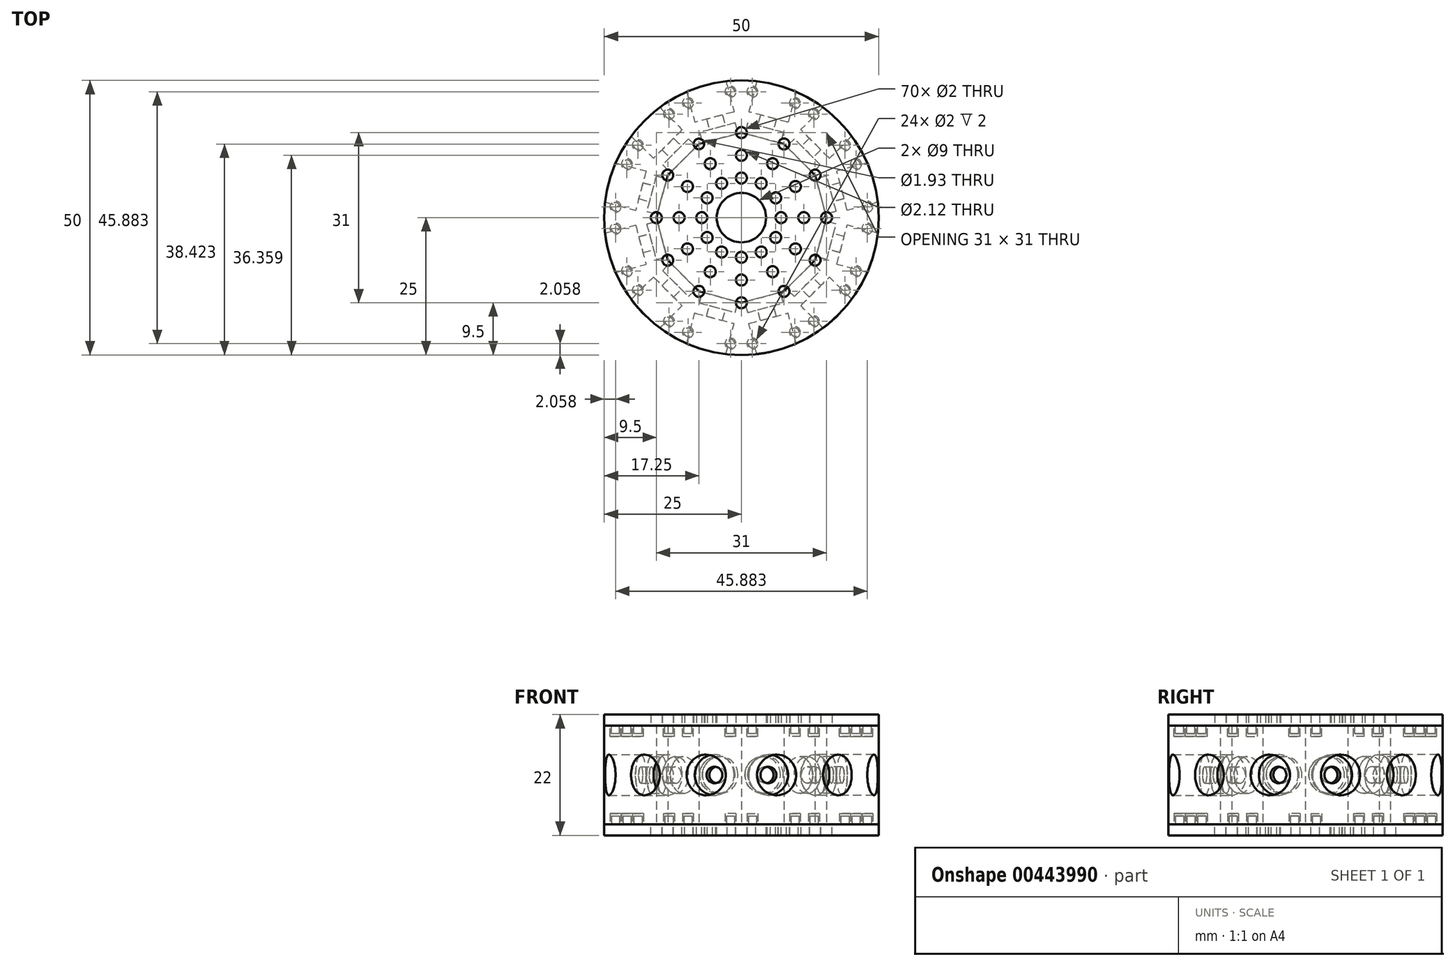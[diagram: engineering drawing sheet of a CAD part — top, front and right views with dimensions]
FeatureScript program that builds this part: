
annotation { "Feature Type Name" : "Feature", "Feature Type Description" : "" }
export const myFeature = defineFeature(function(context is Context, id is Id, definition is map)
    precondition{}
    {
        {
            var Q0;
            Q0=qCreatedBy(makeId("Top.planeOp"),FACE);
            var sketch = newSketch(context, id + "F0", { "sketchPlane" : qUnion([Q0])});
            skCircle(sketch, "E0", {"center": v(0, 0) * mm, "radius": 15.5 * mm, "construction": true});
            skCircle(sketch, "E1", {"center": v(0, 0) * mm, "radius": 25 * mm});
            skLineSegment(sketch, "E2", {"start": v(0, 0) * mm, "end": v(0, 25) * mm});
            skLineSegment(sketch, "E3", {"start": v(0, 0) * mm, "end": v(12.5, 21.65) * mm});
            skLineSegment(sketch, "E4", {"start": v(0, 15.5) * mm, "end": v(7.75, 13.42) * mm});
            skLineSegment(sketch, "E5", {"start": v(7.75, 13.42) * mm, "end": v(13.42, 7.75) * mm});
            skLineSegment(sketch, "E6", {"start": v(13.42, 7.75) * mm, "end": v(15.5, 0) * mm});
            skLineSegment(sketch, "E7", {"start": v(7.75, -13.42) * mm, "end": v(0, -15.5) * mm});
            skLineSegment(sketch, "E8", {"start": v(0, -15.5) * mm, "end": v(-7.75, -13.42) * mm});
            skLineSegment(sketch, "E9", {"start": v(-7.75, -13.42) * mm, "end": v(-13.42, -7.75) * mm});
            skLineSegment(sketch, "E10", {"start": v(-13.42, -7.75) * mm, "end": v(-15.5, 0) * mm});
            skLineSegment(sketch, "E11", {"start": v(-13.42, 7.75) * mm, "end": v(-7.75, 13.42) * mm});
            skLineSegment(sketch, "E12", {"start": v(-7.75, 13.42) * mm, "end": v(0, 15.5) * mm});
            skLineSegment(sketch, "E13", {"start": v(-13.42, 7.75) * mm, "end": v(-15.5, 0) * mm});
            skLineSegment(sketch, "E14.MirrorCS", {"start": v(0, 0) * mm, "end": v(-12.5, 21.65) * mm, "construction": true});
            skLineSegment(sketch, "E15.MirrorCS", {"start": v(0, 0) * mm, "end": v(-21.65, 12.5) * mm, "construction": true});
            skLineSegment(sketch, "E16.MirrorCS", {"start": v(0, 0) * mm, "end": v(-25, 0) * mm, "construction": true});
            skLineSegment(sketch, "E17.MirrorCS", {"start": v(0, 0) * mm, "end": v(-21.65, -12.5) * mm, "construction": true});
            skLineSegment(sketch, "E18.MirrorCS", {"start": v(0, 0) * mm, "end": v(-12.5, -21.65) * mm, "construction": true});
            skLineSegment(sketch, "E19.MirrorCS", {"start": v(0, 0) * mm, "end": v(0, -25) * mm, "construction": true});
            skLineSegment(sketch, "E20.MirrorCS", {"start": v(0, 0) * mm, "end": v(12.5, -21.65) * mm, "construction": true});
            skLineSegment(sketch, "E21.MirrorCS", {"start": v(0, 0) * mm, "end": v(21.65, -12.5) * mm, "construction": true});
            skLineSegment(sketch, "E22.MirrorCS", {"start": v(0, 0) * mm, "end": v(25, 0) * mm, "construction": true});
            skLineSegment(sketch, "E23.MirrorCS", {"start": v(0, 0) * mm, "end": v(21.65, 12.5) * mm, "construction": true});
            skLineSegment(sketch, "E24", {"start": v(7.75, -13.42) * mm, "end": v(13.42, -7.75) * mm});
            skLineSegment(sketch, "E25", {"start": v(13.42, -7.75) * mm, "end": v(15.5, 0) * mm});
            skLineSegment(sketch, "E26", {"start": v(0, 0) * mm, "end": v(14.97, 4.01) * mm, "construction": true});
            skSolve(sketch);
        }
        {
            var Q0;
            {var subQ5=sQuery(id+"F0.wireOp",EDGE,"E4");Q0=makeQuery(id+"F0.imprint","IMPRINT",FACE,{"disambiguationData":[TD([[makeQuery(id+"F0.imprint","IMPRINT",EDGE,{"derivedFrom":subQ5}),1.0]])]});}
            extrude(context, id + "F1", {"entities" : qUnion([Q0]), "depth" : 18 * mm});
        }
        {
            var Q0;
            Q0=makeQuery(id+"F1.opExtrude","SWEPT_FACE",FACE,{"disambiguationData":[OSD([sQuery(id+"F0.wireOp",EDGE,"E4")])]});
            var sketch = newSketch(context, id + "F2", { "sketchPlane" : qUnion([Q0])});
            skLineSegment(sketch, "E27.0", {"start": v(-4.01, 18) * mm, "end": v(4.01, 18) * mm});
            skLineSegment(sketch, "E27.1", {"start": v(-4.01, 18) * mm, "end": v(-4.01, 0) * mm});
            skLineSegment(sketch, "E27.2", {"start": v(-4.01, 0) * mm, "end": v(4.01, 0) * mm});
            skLineSegment(sketch, "E27.3", {"start": v(4.01, 18) * mm, "end": v(4.01, 0) * mm});
            skLineSegment(sketch, "E28", {"start": v(-4.01, 18) * mm, "end": v(4.01, 0) * mm, "construction": true});
            skLineSegment(sketch, "E29", {"start": v(-4.01, 0) * mm, "end": v(4.01, 18) * mm, "construction": true});
            skCircle(sketch, "E30", {"center": v(0, 9) * mm, "radius": 3.35 * mm});
            skCircle(sketch, "E31", {"center": v(0, 9) * mm, "radius": 1.5 * mm});
            skSolve(sketch);
        }
        {
            var Q0;
            Q0=makeQuery(id+"F2.imprint","IMPRINT",FACE,{"disambiguationData":[TD([[makeQuery(id+"F2.imprint","IMPRINT",EDGE,{"derivedFrom":sQuery(id+"F2.wireOp",EDGE,"E30")}),1.0]])]});
            extrude(context, id + "F3", {"entities" : qUnion([Q0]), "operationType" : NewBodyOperationType.REMOVE, "oppositeDirection" : true, "depth" : 2 * mm});
        }
        {
            var Q0;
            Q0=makeQuery(id+"F3.boolean.opBoolean","SPLIT",FACE,{"disambiguationData":[TD([makeQuery(id+"F3.opExtrude","SWEPT_FACE",FACE,{"disambiguationData":[OSD([sQuery(id+"F2.wireOp",EDGE,"E31")])]})])],"derivedFrom":makeQuery(id+"F1.opExtrude","SWEPT_FACE",FACE,{"disambiguationData":[OSD([sQuery(id+"F0.wireOp",EDGE,"E4")])]})});
            extrude(context, id + "F4", {"entities" : qUnion([Q0]), "operationType" : NewBodyOperationType.REMOVE, "oppositeDirection" : true, "depth" : 12 * mm});
        }
        {
            var Q0;
            {var subQ1=sQuery(id+"F0.wireOp",EDGE,"E2");var subQ2=sQuery(id+"F0.wireOp",EDGE,"E4");Q0=makeQuery(id+"F3.boolean.opBoolean","SPLIT",FACE,{"disambiguationData":[TD([makeQuery(id+"F1.opExtrude","SWEPT_FACE",FACE,{"disambiguationData":[OSD([subQ1])]})])],"derivedFrom":makeQuery(id+"F1.opExtrude","SWEPT_FACE",FACE,{"disambiguationData":[OSD([subQ2])]})});}
            cPlane(context, id + "F5", {"entities" : qUnion([Q0]), "cplaneType" : CPlaneType.OFFSET, "offset" : 4 * mm, "oppositeDirection" : true, "width" : 150 * mm, "height" : 150 * mm});
        }
        {
            var Q0;
            Q0=qCreatedBy(id+"F5.planeOp",FACE);
            var sketch = newSketch(context, id + "F6", { "sketchPlane" : qUnion([Q0])});
            skLineSegment(sketch, "E32.0", {"start": v(-4.01, 18) * mm, "end": v(4.01, 18) * mm});
            skLineSegment(sketch, "E32.1", {"start": v(-4.01, 18) * mm, "end": v(-4.01, 0) * mm});
            skLineSegment(sketch, "E32.2", {"start": v(-4.01, 0) * mm, "end": v(4.01, 0) * mm});
            skLineSegment(sketch, "E32.3", {"start": v(4.01, 18) * mm, "end": v(4.01, 0) * mm});
            skLineSegment(sketch, "E33", {"start": v(-4.01, 18) * mm, "end": v(4.01, 0) * mm, "construction": true});
            skLineSegment(sketch, "E34", {"start": v(-4.01, 0) * mm, "end": v(4.01, 18) * mm, "construction": true});
            skCircle(sketch, "E35", {"center": v(0, 9) * mm, "radius": 3.7 * mm});
            skSolve(sketch);
        }
        {
            var Q0;
            Q0=makeQuery(id+"F6.imprint","IMPRINT",FACE,{"disambiguationData":[TD([[makeQuery(id+"F6.imprint","IMPRINT",EDGE,{"derivedFrom":sQuery(id+"F6.wireOp",EDGE,"E35")}),1.0]])]});
            extrude(context, id + "F7", {"entities" : qUnion([Q0]), "operationType" : NewBodyOperationType.REMOVE, "oppositeDirection" : true, "depth" : 12 * mm});
        }
        {
            var Q0;
            Q0=makeQuery(id+"F1.opExtrude","CAP_FACE",FACE,{"disambiguationData":[OSD([sQuery(id+"F0.wireOp",EDGE,"E1"),sQuery(id+"F0.wireOp",EDGE,"E2"),sQuery(id+"F0.wireOp",EDGE,"E3"),sQuery(id+"F0.wireOp",EDGE,"E4")])],"isStart":false});
            var sketch = newSketch(context, id + "F8", { "sketchPlane" : qUnion([Q0])});
            skArc(sketch, "E36.0", {"start": v(12.5, 21.65) * mm, "mid": v(6.47, 24.15) * mm, "end": v(0, 25) * mm, "construction": true});
            skLineSegment(sketch, "E36.1", {"start": v(0, 15.5) * mm, "end": v(0, 25) * mm, "construction": true});
            skLineSegment(sketch, "E36.2", {"start": v(0, 15.5) * mm, "end": v(7.75, 13.42) * mm, "construction": true});
            skLineSegment(sketch, "E36.3", {"start": v(7.75, 13.42) * mm, "end": v(12.5, 21.65) * mm, "construction": true});
            skLineSegment(sketch, "E37", {"start": v(0, 15.5) * mm, "end": v(2.51, 24.87) * mm, "construction": true});
            skLineSegment(sketch, "E38", {"start": v(7.75, 13.42) * mm, "end": v(10.26, 22.8) * mm, "construction": true});
            skLineSegment(sketch, "E39", {"start": v(10.26, 22.8) * mm, "end": v(2.51, 24.87) * mm, "construction": true});
            skLineSegment(sketch, "E40", {"start": v(2, 22.94) * mm, "end": v(9.74, 20.87) * mm, "construction": true});
            skCircle(sketch, "E41", {"center": v(9.74, 20.87) * mm, "radius": 1 * mm});
            skSolve(sketch);
        }
        {
            var Q0;
            Q0=makeQuery(id+"F8.imprint","IMPRINT",FACE,{"disambiguationData":[TD([[makeQuery(id+"F8.imprint","IMPRINT",EDGE,{"derivedFrom":sQuery(id+"F8.wireOp",EDGE,"E41")}),1.0]])]});
            var Q1;
            Q1=sQuery(id+"F8.wireOp",EDGE,"E41");
            extrude(context, id + "F9", {"entities" : qUnion([Q0]), "operationType" : NewBodyOperationType.REMOVE, "surfaceEntities" : qUnion([Q1]), "oppositeDirection" : true, "depth" : 2 * mm});
        }
        {
            var Q0;
            Q0=makeQuery(id+"F1.opExtrude","CAP_FACE",FACE,{"disambiguationData":[OSD([sQuery(id+"F0.wireOp",EDGE,"E1"),sQuery(id+"F0.wireOp",EDGE,"E2"),sQuery(id+"F0.wireOp",EDGE,"E3"),sQuery(id+"F0.wireOp",EDGE,"E4")])],"isStart":true});
            var sketch = newSketch(context, id + "F10", { "sketchPlane" : qUnion([Q0])});
            skArc(sketch, "E42.0", {"start": v(12.5, -21.65) * mm, "mid": v(6.47, -24.15) * mm, "end": v(0, -25) * mm, "construction": true});
            skLineSegment(sketch, "E42.1", {"start": v(7.75, -13.42) * mm, "end": v(12.5, -21.65) * mm, "construction": true});
            skLineSegment(sketch, "E42.2", {"start": v(0, -15.5) * mm, "end": v(7.75, -13.42) * mm, "construction": true});
            skLineSegment(sketch, "E42.3", {"start": v(0, -15.5) * mm, "end": v(0, -25) * mm, "construction": true});
            skLineSegment(sketch, "E43", {"start": v(7.75, -13.42) * mm, "end": v(10.26, -22.8) * mm, "construction": true});
            skLineSegment(sketch, "E44", {"start": v(0, -15.5) * mm, "end": v(2.51, -24.87) * mm, "construction": true});
            skLineSegment(sketch, "E45", {"start": v(2.51, -24.87) * mm, "end": v(10.26, -22.8) * mm, "construction": true});
            skLineSegment(sketch, "E46", {"start": v(9.74, -20.87) * mm, "end": v(2, -22.94) * mm, "construction": true});
            skCircle(sketch, "E47", {"center": v(2, -22.94) * mm, "radius": 1 * mm});
            skSolve(sketch);
        }
        {
            var Q0;
            Q0=makeQuery(id+"F10.imprint","IMPRINT",FACE,{"disambiguationData":[TD([[makeQuery(id+"F10.imprint","IMPRINT",EDGE,{"derivedFrom":sQuery(id+"F10.wireOp",EDGE,"E47")}),1.0]])]});
            extrude(context, id + "F11", {"entities" : qUnion([Q0]), "operationType" : NewBodyOperationType.REMOVE, "oppositeDirection" : true, "depth" : 2 * mm});
        }
        {
            var Q0;
            Q0=makeQuery(id+"F1.opExtrude","SWEPT_BODY",BODY,{"disambiguationData":[OSD([sQuery(id+"F0.wireOp",EDGE,"E1"),sQuery(id+"F0.wireOp",EDGE,"E2"),sQuery(id+"F0.wireOp",EDGE,"E3"),sQuery(id+"F0.wireOp",EDGE,"E4")])]});
            var Q1;
            Q1=sQuery(id+"F0.wireOp",EDGE,"E0");
            circularPattern(context, id + "F12", {"operationType" : NewBodyOperationType.ADD, "entities" : qUnion([Q0]), "axis" : qUnion([Q1]), "angle" : 360 * degree, "instanceCount" : 12, "equalSpace" : true});
        }
        {
            var Q0;
            {var subQ0=makeQuery(id+"F1.opExtrude","CAP_FACE",FACE,{"disambiguationData":[OSD([sQuery(id+"F0.wireOp",EDGE,"E1"),sQuery(id+"F0.wireOp",EDGE,"E2"),sQuery(id+"F0.wireOp",EDGE,"E3"),sQuery(id+"F0.wireOp",EDGE,"E4")])],"isStart":false});Q0=makeQuery(id+"F12.boolean.opBoolean","MERGE",FACE,{"derivedFrom":[subQ0,makeQuery(id+"F12.opPattern","COPY",FACE,{"derivedFrom":subQ0,"instanceName":"1"}),makeQuery(id+"F12.opPattern","COPY",FACE,{"derivedFrom":subQ0,"instanceName":"2"}),makeQuery(id+"F12.opPattern","COPY",FACE,{"derivedFrom":subQ0,"instanceName":"3"}),makeQuery(id+"F12.opPattern","COPY",FACE,{"derivedFrom":subQ0,"instanceName":"4"}),makeQuery(id+"F12.opPattern","COPY",FACE,{"derivedFrom":subQ0,"instanceName":"5"}),makeQuery(id+"F12.opPattern","COPY",FACE,{"derivedFrom":subQ0,"instanceName":"6"}),makeQuery(id+"F12.opPattern","COPY",FACE,{"derivedFrom":subQ0,"instanceName":"7"}),makeQuery(id+"F12.opPattern","COPY",FACE,{"derivedFrom":subQ0,"instanceName":"8"}),makeQuery(id+"F12.opPattern","COPY",FACE,{"derivedFrom":subQ0,"instanceName":"9"}),makeQuery(id+"F12.opPattern","COPY",FACE,{"derivedFrom":subQ0,"instanceName":"10"}),makeQuery(id+"F12.opPattern","COPY",FACE,{"derivedFrom":subQ0,"instanceName":"11"})]});}
            var sketch = newSketch(context, id + "F13", { "sketchPlane" : qUnion([Q0])});
            skCircle(sketch, "E48.0", {"center": v(0, 0) * mm, "radius": 25 * mm});
            skCircle(sketch, "E48.1", {"center": v(-2, 22.94) * mm, "radius": 1 * mm, "construction": true});
            skCircle(sketch, "E48.2", {"center": v(9.74, 20.87) * mm, "radius": 1 * mm, "construction": true});
            skCircle(sketch, "E48.3", {"center": v(18.87, 13.2) * mm, "radius": 1 * mm, "construction": true});
            skCircle(sketch, "E48.4", {"center": v(22.94, 2) * mm, "radius": 1 * mm, "construction": true});
            skCircle(sketch, "E48.5", {"center": v(20.87, -9.74) * mm, "radius": 1 * mm, "construction": true});
            skCircle(sketch, "E48.6", {"center": v(13.2, -18.87) * mm, "radius": 1 * mm, "construction": true});
            skCircle(sketch, "E48.7", {"center": v(2, -22.94) * mm, "radius": 1 * mm, "construction": true});
            skCircle(sketch, "E48.8", {"center": v(-9.74, -20.87) * mm, "radius": 1 * mm, "construction": true});
            skCircle(sketch, "E48.9", {"center": v(-18.87, -13.2) * mm, "radius": 1 * mm, "construction": true});
            skCircle(sketch, "E48.10", {"center": v(-22.94, -2) * mm, "radius": 1 * mm, "construction": true});
            skCircle(sketch, "E48.11", {"center": v(-20.87, 9.74) * mm, "radius": 1 * mm, "construction": true});
            skCircle(sketch, "E48.12", {"center": v(-13.2, 18.87) * mm, "radius": 1 * mm, "construction": true});
            skCircle(sketch, "E49", {"center": v(0, 0) * mm, "radius": 4.5 * mm});
            skCircle(sketch, "E50", {"center": v(-20.87, 9.74) * mm, "radius": 0.75 * mm});
            skCircle(sketch, "E51", {"center": v(-22.94, -2) * mm, "radius": 0.75 * mm});
            skCircle(sketch, "E52", {"center": v(-13.2, 18.87) * mm, "radius": 0.75 * mm});
            skCircle(sketch, "E53", {"center": v(-2, 22.94) * mm, "radius": 0.75 * mm});
            skCircle(sketch, "E54", {"center": v(9.74, 20.87) * mm, "radius": 0.75 * mm});
            skCircle(sketch, "E55", {"center": v(18.87, 13.2) * mm, "radius": 0.75 * mm});
            skCircle(sketch, "E56", {"center": v(22.94, 2) * mm, "radius": 0.75 * mm});
            skCircle(sketch, "E57", {"center": v(20.87, -9.74) * mm, "radius": 0.75 * mm});
            skCircle(sketch, "E58", {"center": v(13.2, -18.87) * mm, "radius": 0.75 * mm});
            skCircle(sketch, "E59", {"center": v(2, -22.94) * mm, "radius": 0.75 * mm});
            skCircle(sketch, "E60", {"center": v(-9.74, -20.87) * mm, "radius": 0.75 * mm});
            skCircle(sketch, "E61", {"center": v(-18.87, -13.2) * mm, "radius": 0.75 * mm});
            skLineSegment(sketch, "E62", {"start": v(13.42, 7.75) * mm, "end": v(7.75, 13.42) * mm, "construction": true});
            skLineSegment(sketch, "E63", {"start": v(7.75, 13.42) * mm, "end": v(0, 15.5) * mm, "construction": true});
            skLineSegment(sketch, "E64", {"start": v(0, 15.5) * mm, "end": v(-7.75, 13.42) * mm, "construction": true});
            skLineSegment(sketch, "E65", {"start": v(-7.75, 13.42) * mm, "end": v(-13.42, 7.75) * mm, "construction": true});
            skLineSegment(sketch, "E66", {"start": v(-13.42, 7.75) * mm, "end": v(-15.5, 0) * mm, "construction": true});
            skLineSegment(sketch, "E67", {"start": v(-15.5, 0) * mm, "end": v(-13.42, -7.75) * mm, "construction": true});
            skLineSegment(sketch, "E68", {"start": v(-13.42, -7.75) * mm, "end": v(-7.75, -13.42) * mm, "construction": true});
            skLineSegment(sketch, "E69", {"start": v(-7.75, -13.42) * mm, "end": v(0, -15.5) * mm, "construction": true});
            skLineSegment(sketch, "E70", {"start": v(0, -15.5) * mm, "end": v(7.75, -13.42) * mm, "construction": true});
            skLineSegment(sketch, "E71", {"start": v(7.75, -13.42) * mm, "end": v(13.42, -7.75) * mm, "construction": true});
            skLineSegment(sketch, "E72", {"start": v(13.42, -7.75) * mm, "end": v(15.5, 0) * mm, "construction": true});
            skLineSegment(sketch, "E73", {"start": v(15.5, 0) * mm, "end": v(13.42, 7.75) * mm, "construction": true});
            skLineSegment(sketch, "E74.0", {"start": v(9.84, 5.68) * mm, "end": v(5.68, 9.84) * mm, "construction": true});
            skLineSegment(sketch, "E74.1", {"start": v(-11.36, 0) * mm, "end": v(-9.84, -5.68) * mm, "construction": true});
            skLineSegment(sketch, "E74.2", {"start": v(-9.84, 5.68) * mm, "end": v(-11.36, 0) * mm, "construction": true});
            skLineSegment(sketch, "E74.3", {"start": v(-5.68, 9.84) * mm, "end": v(-9.84, 5.68) * mm, "construction": true});
            skLineSegment(sketch, "E74.4", {"start": v(0, 11.36) * mm, "end": v(-5.68, 9.84) * mm, "construction": true});
            skLineSegment(sketch, "E74.5", {"start": v(-9.84, -5.68) * mm, "end": v(-5.68, -9.84) * mm, "construction": true});
            skLineSegment(sketch, "E74.6", {"start": v(5.68, 9.84) * mm, "end": v(0, 11.36) * mm, "construction": true});
            skLineSegment(sketch, "E74.7", {"start": v(-5.68, -9.84) * mm, "end": v(0, -11.36) * mm, "construction": true});
            skLineSegment(sketch, "E74.8", {"start": v(0, -11.36) * mm, "end": v(5.68, -9.84) * mm, "construction": true});
            skLineSegment(sketch, "E74.9", {"start": v(5.68, -9.84) * mm, "end": v(9.84, -5.68) * mm, "construction": true});
            skLineSegment(sketch, "E74.10", {"start": v(9.84, -5.68) * mm, "end": v(11.36, 0) * mm, "construction": true});
            skLineSegment(sketch, "E74.11", {"start": v(11.36, 0) * mm, "end": v(9.84, 5.68) * mm, "construction": true});
            skLineSegment(sketch, "E75.0", {"start": v(6.25, 3.6) * mm, "end": v(3.6, 6.25) * mm, "construction": true});
            skLineSegment(sketch, "E75.1", {"start": v(-7.22, 0) * mm, "end": v(-6.25, -3.6) * mm, "construction": true});
            skLineSegment(sketch, "E75.2", {"start": v(-6.25, 3.6) * mm, "end": v(-7.22, 0) * mm, "construction": true});
            skLineSegment(sketch, "E75.3", {"start": v(-3.6, 6.25) * mm, "end": v(-6.25, 3.6) * mm, "construction": true});
            skLineSegment(sketch, "E75.4", {"start": v(0, 7.22) * mm, "end": v(-3.6, 6.25) * mm, "construction": true});
            skLineSegment(sketch, "E75.5", {"start": v(-6.25, -3.6) * mm, "end": v(-3.6, -6.25) * mm, "construction": true});
            skLineSegment(sketch, "E75.6", {"start": v(3.6, 6.25) * mm, "end": v(0, 7.22) * mm, "construction": true});
            skLineSegment(sketch, "E75.7", {"start": v(-3.6, -6.25) * mm, "end": v(0, -7.22) * mm, "construction": true});
            skLineSegment(sketch, "E75.8", {"start": v(0, -7.22) * mm, "end": v(3.6, -6.25) * mm, "construction": true});
            skLineSegment(sketch, "E75.9", {"start": v(3.6, -6.25) * mm, "end": v(6.25, -3.6) * mm, "construction": true});
            skLineSegment(sketch, "E75.10", {"start": v(6.25, -3.6) * mm, "end": v(7.22, 0) * mm, "construction": true});
            skLineSegment(sketch, "E75.11", {"start": v(7.22, 0) * mm, "end": v(6.25, 3.6) * mm, "construction": true});
            skCircle(sketch, "E76", {"center": v(13.42, 7.75) * mm, "radius": 1 * mm});
            skCircle(sketch, "E77", {"center": v(7.75, 13.42) * mm, "radius": 1 * mm});
            skCircle(sketch, "E78", {"center": v(0, 15.5) * mm, "radius": 1 * mm});
            skCircle(sketch, "E79", {"center": v(-7.75, 13.42) * mm, "radius": 0.97 * mm});
            skCircle(sketch, "E80", {"center": v(-13.42, 7.75) * mm, "radius": 1 * mm});
            skCircle(sketch, "E81", {"center": v(-15.5, 0) * mm, "radius": 1 * mm});
            skCircle(sketch, "E82", {"center": v(-13.42, -7.75) * mm, "radius": 1 * mm});
            skCircle(sketch, "E83", {"center": v(-7.75, -13.42) * mm, "radius": 1 * mm});
            skCircle(sketch, "E84", {"center": v(0, -15.5) * mm, "radius": 1 * mm});
            skCircle(sketch, "E85", {"center": v(7.75, -13.42) * mm, "radius": 1 * mm});
            skCircle(sketch, "E86", {"center": v(13.42, -7.75) * mm, "radius": 1 * mm});
            skCircle(sketch, "E87", {"center": v(15.5, 0) * mm, "radius": 1 * mm});
            skCircle(sketch, "E88", {"center": v(11.36, 0) * mm, "radius": 1 * mm});
            skCircle(sketch, "E89", {"center": v(9.84, 5.68) * mm, "radius": 1 * mm});
            skCircle(sketch, "E90", {"center": v(5.68, 9.84) * mm, "radius": 1 * mm});
            skCircle(sketch, "E91", {"center": v(0, 11.36) * mm, "radius": 1 * mm});
            skCircle(sketch, "E92", {"center": v(-5.68, 9.84) * mm, "radius": 1 * mm});
            skCircle(sketch, "E93", {"center": v(-9.84, 5.68) * mm, "radius": 1 * mm});
            skCircle(sketch, "E94", {"center": v(-11.36, 0) * mm, "radius": 1 * mm});
            skCircle(sketch, "E95", {"center": v(-9.84, -5.68) * mm, "radius": 1 * mm});
            skCircle(sketch, "E96", {"center": v(-5.68, -9.84) * mm, "radius": 1 * mm});
            skCircle(sketch, "E97", {"center": v(0, -11.36) * mm, "radius": 1 * mm});
            skCircle(sketch, "E98", {"center": v(5.68, -9.84) * mm, "radius": 1 * mm});
            skCircle(sketch, "E99", {"center": v(9.84, -5.68) * mm, "radius": 1 * mm});
            skCircle(sketch, "E100", {"center": v(7.22, 0) * mm, "radius": 1 * mm});
            skCircle(sketch, "E101", {"center": v(6.25, 3.6) * mm, "radius": 1 * mm});
            skCircle(sketch, "E102", {"center": v(3.6, 6.25) * mm, "radius": 1 * mm});
            skCircle(sketch, "E103", {"center": v(0, 7.22) * mm, "radius": 1 * mm});
            skCircle(sketch, "E104", {"center": v(-3.6, 6.25) * mm, "radius": 1 * mm});
            skCircle(sketch, "E105", {"center": v(-6.25, 3.6) * mm, "radius": 1 * mm});
            skCircle(sketch, "E106", {"center": v(-7.22, 0) * mm, "radius": 1 * mm});
            skCircle(sketch, "E107", {"center": v(-6.25, -3.6) * mm, "radius": 1 * mm});
            skCircle(sketch, "E108", {"center": v(-3.6, -6.25) * mm, "radius": 1 * mm});
            skCircle(sketch, "E109", {"center": v(0, -7.22) * mm, "radius": 1 * mm});
            skCircle(sketch, "E110", {"center": v(3.6, -6.25) * mm, "radius": 1 * mm});
            skCircle(sketch, "E111", {"center": v(6.25, -3.6) * mm, "radius": 1 * mm});
            skSolve(sketch);
        }
        {
            var Q0;
            Q0=makeQuery(id+"F13.imprint","IMPRINT",FACE,{"disambiguationData":[TD([[makeQuery(id+"F13.imprint","IMPRINT",EDGE,{"derivedFrom":sQuery(id+"F13.wireOp",EDGE,"E48.0")}),1.0]])]});
            var Q1;
            Q1=makeQuery(id+"F13.imprint","IMPRINT",FACE,{"disambiguationData":[TD([[makeQuery(id+"F13.imprint","IMPRINT",EDGE,{"derivedFrom":sQuery(id+"F13.wireOp",EDGE,"E50")}),-1.0]])]});
            var Q2;
            Q2=makeQuery(id+"F13.imprint","IMPRINT",FACE,{"disambiguationData":[TD([[makeQuery(id+"F13.imprint","IMPRINT",EDGE,{"derivedFrom":sQuery(id+"F13.wireOp",EDGE,"E51")}),-1.0]])]});
            var Q3;
            Q3=makeQuery(id+"F13.imprint","IMPRINT",FACE,{"disambiguationData":[TD([[makeQuery(id+"F13.imprint","IMPRINT",EDGE,{"derivedFrom":sQuery(id+"F13.wireOp",EDGE,"E49")}),-1.0]])]});
            var Q4;
            Q4=makeQuery(id+"F13.imprint","IMPRINT",FACE,{"disambiguationData":[TD([[makeQuery(id+"F13.imprint","IMPRINT",EDGE,{"derivedFrom":sQuery(id+"F13.wireOp",EDGE,"E61")}),-1.0]])]});
            var Q5;
            Q5=makeQuery(id+"F13.imprint","IMPRINT",FACE,{"disambiguationData":[TD([[makeQuery(id+"F13.imprint","IMPRINT",EDGE,{"derivedFrom":sQuery(id+"F13.wireOp",EDGE,"E60")}),-1.0]])]});
            var Q6;
            Q6=makeQuery(id+"F13.imprint","IMPRINT",FACE,{"disambiguationData":[TD([[makeQuery(id+"F13.imprint","IMPRINT",EDGE,{"derivedFrom":sQuery(id+"F13.wireOp",EDGE,"E59")}),-1.0]])]});
            var Q7;
            Q7=makeQuery(id+"F13.imprint","IMPRINT",FACE,{"disambiguationData":[TD([[makeQuery(id+"F13.imprint","IMPRINT",EDGE,{"derivedFrom":sQuery(id+"F13.wireOp",EDGE,"E58")}),-1.0]])]});
            var Q8;
            Q8=makeQuery(id+"F13.imprint","IMPRINT",FACE,{"disambiguationData":[TD([[makeQuery(id+"F13.imprint","IMPRINT",EDGE,{"derivedFrom":sQuery(id+"F13.wireOp",EDGE,"E57")}),-1.0]])]});
            var Q9;
            Q9=makeQuery(id+"F13.imprint","IMPRINT",FACE,{"disambiguationData":[TD([[makeQuery(id+"F13.imprint","IMPRINT",EDGE,{"derivedFrom":sQuery(id+"F13.wireOp",EDGE,"E56")}),-1.0]])]});
            var Q10;
            Q10=makeQuery(id+"F13.imprint","IMPRINT",FACE,{"disambiguationData":[TD([[makeQuery(id+"F13.imprint","IMPRINT",EDGE,{"derivedFrom":sQuery(id+"F13.wireOp",EDGE,"E55")}),-1.0]])]});
            var Q11;
            Q11=makeQuery(id+"F13.imprint","IMPRINT",FACE,{"disambiguationData":[TD([[makeQuery(id+"F13.imprint","IMPRINT",EDGE,{"derivedFrom":sQuery(id+"F13.wireOp",EDGE,"E54")}),-1.0]])]});
            var Q12;
            Q12=makeQuery(id+"F13.imprint","IMPRINT",FACE,{"disambiguationData":[TD([[makeQuery(id+"F13.imprint","IMPRINT",EDGE,{"derivedFrom":sQuery(id+"F13.wireOp",EDGE,"E53")}),-1.0]])]});
            var Q13;
            Q13=makeQuery(id+"F13.imprint","IMPRINT",FACE,{"disambiguationData":[TD([[makeQuery(id+"F13.imprint","IMPRINT",EDGE,{"derivedFrom":sQuery(id+"F13.wireOp",EDGE,"E52")}),-1.0]])]});
            var Q14;
            Q14=makeQuery(id+"F13.imprint","IMPRINT",FACE,{"disambiguationData":[TD([[makeQuery(id+"F13.imprint","IMPRINT",EDGE,{"derivedFrom":sQuery(id+"F13.wireOp",EDGE,"E51")}),1.0]])]});
            var Q15;
            Q15=makeQuery(id+"F13.imprint","IMPRINT",FACE,{"disambiguationData":[TD([[makeQuery(id+"F13.imprint","IMPRINT",EDGE,{"derivedFrom":sQuery(id+"F13.wireOp",EDGE,"E50")}),1.0]])]});
            var Q16;
            Q16=makeQuery(id+"F13.imprint","IMPRINT",FACE,{"disambiguationData":[TD([[makeQuery(id+"F13.imprint","IMPRINT",EDGE,{"derivedFrom":sQuery(id+"F13.wireOp",EDGE,"E61")}),1.0]])]});
            var Q17;
            Q17=makeQuery(id+"F13.imprint","IMPRINT",FACE,{"disambiguationData":[TD([[makeQuery(id+"F13.imprint","IMPRINT",EDGE,{"derivedFrom":sQuery(id+"F13.wireOp",EDGE,"E57")}),1.0]])]});
            var Q18;
            Q18=makeQuery(id+"F13.imprint","IMPRINT",FACE,{"disambiguationData":[TD([[makeQuery(id+"F13.imprint","IMPRINT",EDGE,{"derivedFrom":sQuery(id+"F13.wireOp",EDGE,"E56")}),1.0]])]});
            var Q19;
            Q19=makeQuery(id+"F13.imprint","IMPRINT",FACE,{"disambiguationData":[TD([[makeQuery(id+"F13.imprint","IMPRINT",EDGE,{"derivedFrom":sQuery(id+"F13.wireOp",EDGE,"E55")}),1.0]])]});
            var Q20;
            Q20=makeQuery(id+"F13.imprint","IMPRINT",FACE,{"disambiguationData":[TD([[makeQuery(id+"F13.imprint","IMPRINT",EDGE,{"derivedFrom":sQuery(id+"F13.wireOp",EDGE,"E60")}),1.0]])]});
            var Q21;
            Q21=makeQuery(id+"F13.imprint","IMPRINT",FACE,{"disambiguationData":[TD([[makeQuery(id+"F13.imprint","IMPRINT",EDGE,{"derivedFrom":sQuery(id+"F13.wireOp",EDGE,"E59")}),1.0]])]});
            var Q22;
            Q22=makeQuery(id+"F13.imprint","IMPRINT",FACE,{"disambiguationData":[TD([[makeQuery(id+"F13.imprint","IMPRINT",EDGE,{"derivedFrom":sQuery(id+"F13.wireOp",EDGE,"E58")}),1.0]])]});
            var Q23;
            Q23=makeQuery(id+"F13.imprint","IMPRINT",FACE,{"disambiguationData":[TD([[makeQuery(id+"F13.imprint","IMPRINT",EDGE,{"derivedFrom":sQuery(id+"F13.wireOp",EDGE,"E53")}),1.0]])]});
            var Q24;
            Q24=makeQuery(id+"F13.imprint","IMPRINT",FACE,{"disambiguationData":[TD([[makeQuery(id+"F13.imprint","IMPRINT",EDGE,{"derivedFrom":sQuery(id+"F13.wireOp",EDGE,"E54")}),1.0]])]});
            var Q25;
            Q25=makeQuery(id+"F13.imprint","IMPRINT",FACE,{"disambiguationData":[TD([[makeQuery(id+"F13.imprint","IMPRINT",EDGE,{"derivedFrom":sQuery(id+"F13.wireOp",EDGE,"E52")}),1.0]])]});
            extrude(context, id + "F14", {"entities" : qUnion([Q0, Q1, Q2, Q3, Q4, Q5, Q6, Q7, Q8, Q9, Q10, Q11, Q12, Q13, Q14, Q15, Q16, Q17, Q18, Q19, Q20, Q21, Q22, Q23, Q24, Q25]), "depth" : 2 * mm});
        }
        {
            var Q0;
            Q0=makeQuery(id+"F13.imprint","IMPRINT",FACE,{"disambiguationData":[TD([[makeQuery(id+"F13.imprint","IMPRINT",EDGE,{"derivedFrom":sQuery(id+"F13.wireOp",EDGE,"E52")}),1.0]])]});
            var Q1;
            Q1=makeQuery(id+"F13.imprint","IMPRINT",FACE,{"disambiguationData":[TD([[makeQuery(id+"F13.imprint","IMPRINT",EDGE,{"derivedFrom":sQuery(id+"F13.wireOp",EDGE,"E53")}),1.0]])]});
            var Q2;
            Q2=makeQuery(id+"F13.imprint","IMPRINT",FACE,{"disambiguationData":[TD([[makeQuery(id+"F13.imprint","IMPRINT",EDGE,{"derivedFrom":sQuery(id+"F13.wireOp",EDGE,"E54")}),1.0]])]});
            var Q3;
            Q3=makeQuery(id+"F13.imprint","IMPRINT",FACE,{"disambiguationData":[TD([[makeQuery(id+"F13.imprint","IMPRINT",EDGE,{"derivedFrom":sQuery(id+"F13.wireOp",EDGE,"E50")}),1.0]])]});
            var Q4;
            Q4=makeQuery(id+"F13.imprint","IMPRINT",FACE,{"disambiguationData":[TD([[makeQuery(id+"F13.imprint","IMPRINT",EDGE,{"derivedFrom":sQuery(id+"F13.wireOp",EDGE,"E51")}),1.0]])]});
            var Q5;
            Q5=makeQuery(id+"F13.imprint","IMPRINT",FACE,{"disambiguationData":[TD([[makeQuery(id+"F13.imprint","IMPRINT",EDGE,{"derivedFrom":sQuery(id+"F13.wireOp",EDGE,"E61")}),1.0]])]});
            var Q6;
            Q6=makeQuery(id+"F13.imprint","IMPRINT",FACE,{"disambiguationData":[TD([[makeQuery(id+"F13.imprint","IMPRINT",EDGE,{"derivedFrom":sQuery(id+"F13.wireOp",EDGE,"E60")}),1.0]])]});
            var Q7;
            Q7=makeQuery(id+"F13.imprint","IMPRINT",FACE,{"disambiguationData":[TD([[makeQuery(id+"F13.imprint","IMPRINT",EDGE,{"derivedFrom":sQuery(id+"F13.wireOp",EDGE,"E59")}),1.0]])]});
            var Q8;
            Q8=makeQuery(id+"F13.imprint","IMPRINT",FACE,{"disambiguationData":[TD([[makeQuery(id+"F13.imprint","IMPRINT",EDGE,{"derivedFrom":sQuery(id+"F13.wireOp",EDGE,"E58")}),1.0]])]});
            var Q9;
            Q9=makeQuery(id+"F13.imprint","IMPRINT",FACE,{"disambiguationData":[TD([[makeQuery(id+"F13.imprint","IMPRINT",EDGE,{"derivedFrom":sQuery(id+"F13.wireOp",EDGE,"E57")}),1.0]])]});
            var Q10;
            Q10=makeQuery(id+"F13.imprint","IMPRINT",FACE,{"disambiguationData":[TD([[makeQuery(id+"F13.imprint","IMPRINT",EDGE,{"derivedFrom":sQuery(id+"F13.wireOp",EDGE,"E56")}),1.0]])]});
            var Q11;
            Q11=makeQuery(id+"F13.imprint","IMPRINT",FACE,{"disambiguationData":[TD([[makeQuery(id+"F13.imprint","IMPRINT",EDGE,{"derivedFrom":sQuery(id+"F13.wireOp",EDGE,"E55")}),1.0]])]});
            extrude(context, id + "F15", {"entities" : qUnion([Q0, Q1, Q2, Q3, Q4, Q5, Q6, Q7, Q8, Q9, Q10, Q11]), "operationType" : NewBodyOperationType.ADD, "oppositeDirection" : true, "depth" : 1.5 * mm});
        }
        {
            var Q0;
            {var subQ0=makeQuery(id+"F1.opExtrude","CAP_FACE",FACE,{"disambiguationData":[OSD([sQuery(id+"F0.wireOp",EDGE,"E1"),sQuery(id+"F0.wireOp",EDGE,"E2"),sQuery(id+"F0.wireOp",EDGE,"E3"),sQuery(id+"F0.wireOp",EDGE,"E4")])],"isStart":true});Q0=makeQuery(id+"F12.boolean.opBoolean","MERGE",FACE,{"derivedFrom":[subQ0,makeQuery(id+"F12.opPattern","COPY",FACE,{"derivedFrom":subQ0,"instanceName":"1"}),makeQuery(id+"F12.opPattern","COPY",FACE,{"derivedFrom":subQ0,"instanceName":"2"}),makeQuery(id+"F12.opPattern","COPY",FACE,{"derivedFrom":subQ0,"instanceName":"3"}),makeQuery(id+"F12.opPattern","COPY",FACE,{"derivedFrom":subQ0,"instanceName":"4"}),makeQuery(id+"F12.opPattern","COPY",FACE,{"derivedFrom":subQ0,"instanceName":"5"}),makeQuery(id+"F12.opPattern","COPY",FACE,{"derivedFrom":subQ0,"instanceName":"6"}),makeQuery(id+"F12.opPattern","COPY",FACE,{"derivedFrom":subQ0,"instanceName":"7"}),makeQuery(id+"F12.opPattern","COPY",FACE,{"derivedFrom":subQ0,"instanceName":"8"}),makeQuery(id+"F12.opPattern","COPY",FACE,{"derivedFrom":subQ0,"instanceName":"9"}),makeQuery(id+"F12.opPattern","COPY",FACE,{"derivedFrom":subQ0,"instanceName":"10"}),makeQuery(id+"F12.opPattern","COPY",FACE,{"derivedFrom":subQ0,"instanceName":"11"})]});}
            var sketch = newSketch(context, id + "F16", { "sketchPlane" : qUnion([Q0])});
            skCircle(sketch, "E112.0", {"center": v(-9.74, -20.87) * mm, "radius": 1 * mm, "construction": true});
            skCircle(sketch, "E112.1", {"center": v(-18.87, -13.2) * mm, "radius": 1 * mm, "construction": true});
            skCircle(sketch, "E112.2", {"center": v(-22.94, -2) * mm, "radius": 1 * mm, "construction": true});
            skCircle(sketch, "E112.3", {"center": v(-20.87, 9.74) * mm, "radius": 1 * mm, "construction": true});
            skCircle(sketch, "E112.4", {"center": v(-13.2, 18.87) * mm, "radius": 1 * mm, "construction": true});
            skCircle(sketch, "E112.5", {"center": v(-2, 22.94) * mm, "radius": 1 * mm, "construction": true});
            skCircle(sketch, "E112.6", {"center": v(9.74, 20.87) * mm, "radius": 1 * mm, "construction": true});
            skCircle(sketch, "E112.7", {"center": v(18.87, 13.2) * mm, "radius": 1 * mm, "construction": true});
            skCircle(sketch, "E112.8", {"center": v(22.94, 2) * mm, "radius": 1 * mm, "construction": true});
            skCircle(sketch, "E112.9", {"center": v(20.87, -9.74) * mm, "radius": 1 * mm, "construction": true});
            skCircle(sketch, "E112.10", {"center": v(13.2, -18.87) * mm, "radius": 1 * mm, "construction": true});
            skCircle(sketch, "E112.11", {"center": v(2, -22.94) * mm, "radius": 1 * mm, "construction": true});
            skCircle(sketch, "E113.0", {"center": v(0, 0) * mm, "radius": 25 * mm});
            skCircle(sketch, "E114", {"center": v(0, 0) * mm, "radius": 4.5 * mm});
            skCircle(sketch, "E115", {"center": v(-18.87, -13.2) * mm, "radius": 0.75 * mm});
            skCircle(sketch, "E116", {"center": v(-9.74, -20.87) * mm, "radius": 0.75 * mm});
            skCircle(sketch, "E117", {"center": v(2, -22.94) * mm, "radius": 0.75 * mm});
            skCircle(sketch, "E118", {"center": v(13.2, -18.87) * mm, "radius": 0.75 * mm});
            skCircle(sketch, "E119", {"center": v(20.87, -9.74) * mm, "radius": 0.75 * mm});
            skCircle(sketch, "E120", {"center": v(22.94, 2) * mm, "radius": 0.75 * mm});
            skCircle(sketch, "E121", {"center": v(18.87, 13.2) * mm, "radius": 0.75 * mm});
            skCircle(sketch, "E122", {"center": v(9.74, 20.87) * mm, "radius": 0.75 * mm});
            skCircle(sketch, "E123", {"center": v(-2, 22.94) * mm, "radius": 0.75 * mm});
            skCircle(sketch, "E124", {"center": v(-13.2, 18.87) * mm, "radius": 0.75 * mm});
            skCircle(sketch, "E125", {"center": v(-20.87, 9.74) * mm, "radius": 0.75 * mm});
            skCircle(sketch, "E126", {"center": v(-22.94, -2) * mm, "radius": 0.75 * mm});
            skLineSegment(sketch, "E127", {"start": v(-13.42, -7.75) * mm, "end": v(-7.75, -13.42) * mm, "construction": true});
            skLineSegment(sketch, "E128", {"start": v(-7.75, -13.42) * mm, "end": v(0, -15.5) * mm, "construction": true});
            skLineSegment(sketch, "E129", {"start": v(0, -15.5) * mm, "end": v(7.75, -13.42) * mm, "construction": true});
            skLineSegment(sketch, "E130", {"start": v(7.75, -13.42) * mm, "end": v(13.42, -7.75) * mm, "construction": true});
            skLineSegment(sketch, "E131", {"start": v(13.42, -7.75) * mm, "end": v(15.5, 0) * mm, "construction": true});
            skLineSegment(sketch, "E132", {"start": v(15.5, 0) * mm, "end": v(13.42, 7.75) * mm, "construction": true});
            skLineSegment(sketch, "E133", {"start": v(13.42, 7.75) * mm, "end": v(7.75, 13.42) * mm, "construction": true});
            skLineSegment(sketch, "E134", {"start": v(7.75, 13.42) * mm, "end": v(0, 15.5) * mm, "construction": true});
            skLineSegment(sketch, "E135", {"start": v(0, 15.5) * mm, "end": v(-7.75, 13.42) * mm, "construction": true});
            skLineSegment(sketch, "E136", {"start": v(-7.75, 13.42) * mm, "end": v(-13.42, 7.75) * mm, "construction": true});
            skLineSegment(sketch, "E137", {"start": v(-13.42, 7.75) * mm, "end": v(-15.5, 0) * mm, "construction": true});
            skLineSegment(sketch, "E138", {"start": v(-15.5, 0) * mm, "end": v(-13.42, -7.75) * mm, "construction": true});
            skLineSegment(sketch, "E139.0", {"start": v(-11.36, 0) * mm, "end": v(-9.84, -5.68) * mm, "construction": true});
            skLineSegment(sketch, "E139.1", {"start": v(9.84, -5.68) * mm, "end": v(11.36, 0) * mm, "construction": true});
            skLineSegment(sketch, "E139.2", {"start": v(5.68, -9.84) * mm, "end": v(9.84, -5.68) * mm, "construction": true});
            skLineSegment(sketch, "E139.3", {"start": v(0, -11.36) * mm, "end": v(5.68, -9.84) * mm, "construction": true});
            skLineSegment(sketch, "E139.4", {"start": v(-5.68, -9.84) * mm, "end": v(0, -11.36) * mm, "construction": true});
            skLineSegment(sketch, "E139.5", {"start": v(11.36, 0) * mm, "end": v(9.84, 5.68) * mm, "construction": true});
            skLineSegment(sketch, "E139.6", {"start": v(-9.84, -5.68) * mm, "end": v(-5.68, -9.84) * mm, "construction": true});
            skLineSegment(sketch, "E139.7", {"start": v(9.84, 5.68) * mm, "end": v(5.68, 9.84) * mm, "construction": true});
            skLineSegment(sketch, "E139.8", {"start": v(5.68, 9.84) * mm, "end": v(0, 11.36) * mm, "construction": true});
            skLineSegment(sketch, "E139.9", {"start": v(0, 11.36) * mm, "end": v(-5.68, 9.84) * mm, "construction": true});
            skLineSegment(sketch, "E139.10", {"start": v(-5.68, 9.84) * mm, "end": v(-9.84, 5.68) * mm, "construction": true});
            skLineSegment(sketch, "E139.11", {"start": v(-9.84, 5.68) * mm, "end": v(-11.36, 0) * mm, "construction": true});
            skLineSegment(sketch, "E140.0", {"start": v(-7.22, 0) * mm, "end": v(-6.25, -3.6) * mm, "construction": true});
            skLineSegment(sketch, "E140.1", {"start": v(6.25, -3.6) * mm, "end": v(7.22, 0) * mm, "construction": true});
            skLineSegment(sketch, "E140.2", {"start": v(3.6, -6.25) * mm, "end": v(6.25, -3.6) * mm, "construction": true});
            skLineSegment(sketch, "E140.3", {"start": v(0, -7.22) * mm, "end": v(3.6, -6.25) * mm, "construction": true});
            skLineSegment(sketch, "E140.4", {"start": v(-3.6, -6.25) * mm, "end": v(0, -7.22) * mm, "construction": true});
            skLineSegment(sketch, "E140.5", {"start": v(7.22, 0) * mm, "end": v(6.25, 3.6) * mm, "construction": true});
            skLineSegment(sketch, "E140.6", {"start": v(-6.25, -3.6) * mm, "end": v(-3.6, -6.25) * mm, "construction": true});
            skLineSegment(sketch, "E140.7", {"start": v(6.25, 3.6) * mm, "end": v(3.6, 6.25) * mm, "construction": true});
            skLineSegment(sketch, "E140.8", {"start": v(3.6, 6.25) * mm, "end": v(0, 7.22) * mm, "construction": true});
            skLineSegment(sketch, "E140.9", {"start": v(0, 7.22) * mm, "end": v(-3.6, 6.25) * mm, "construction": true});
            skLineSegment(sketch, "E140.10", {"start": v(-3.6, 6.25) * mm, "end": v(-6.25, 3.6) * mm, "construction": true});
            skLineSegment(sketch, "E140.11", {"start": v(-6.25, 3.6) * mm, "end": v(-7.22, 0) * mm, "construction": true});
            skCircle(sketch, "E141", {"center": v(-13.42, -7.75) * mm, "radius": 1 * mm});
            skCircle(sketch, "E142", {"center": v(-7.75, -13.42) * mm, "radius": 1 * mm});
            skCircle(sketch, "E143", {"center": v(0, -15.5) * mm, "radius": 1 * mm});
            skCircle(sketch, "E144", {"center": v(7.75, -13.42) * mm, "radius": 1 * mm});
            skCircle(sketch, "E145", {"center": v(13.42, -7.75) * mm, "radius": 1 * mm});
            skCircle(sketch, "E146", {"center": v(15.5, 0) * mm, "radius": 1 * mm});
            skCircle(sketch, "E147", {"center": v(13.42, 7.75) * mm, "radius": 1 * mm});
            skCircle(sketch, "E148", {"center": v(7.75, 13.42) * mm, "radius": 1 * mm});
            skCircle(sketch, "E149", {"center": v(0, 15.5) * mm, "radius": 1 * mm});
            skCircle(sketch, "E150", {"center": v(-7.75, 13.42) * mm, "radius": 1 * mm});
            skCircle(sketch, "E151", {"center": v(-13.42, 7.75) * mm, "radius": 1 * mm});
            skCircle(sketch, "E152", {"center": v(-15.5, 0) * mm, "radius": 1 * mm});
            skCircle(sketch, "E153", {"center": v(0, -11.36) * mm, "radius": 1.06 * mm});
            skCircle(sketch, "E154", {"center": v(5.68, -9.84) * mm, "radius": 1 * mm});
            skCircle(sketch, "E155", {"center": v(9.84, -5.68) * mm, "radius": 1 * mm});
            skCircle(sketch, "E156", {"center": v(11.36, 0) * mm, "radius": 1 * mm});
            skCircle(sketch, "E157", {"center": v(9.84, 5.68) * mm, "radius": 1 * mm});
            skCircle(sketch, "E158", {"center": v(5.68, 9.84) * mm, "radius": 1 * mm});
            skCircle(sketch, "E159", {"center": v(0, 11.36) * mm, "radius": 1 * mm});
            skCircle(sketch, "E160", {"center": v(-5.68, 9.84) * mm, "radius": 1 * mm});
            skCircle(sketch, "E161", {"center": v(-5.68, -9.84) * mm, "radius": 1 * mm});
            skCircle(sketch, "E162", {"center": v(-9.84, -5.68) * mm, "radius": 1 * mm});
            skCircle(sketch, "E163", {"center": v(-11.36, 0) * mm, "radius": 1 * mm});
            skCircle(sketch, "E164", {"center": v(-9.84, 5.68) * mm, "radius": 1 * mm});
            skCircle(sketch, "E165", {"center": v(-6.25, -3.6) * mm, "radius": 1 * mm});
            skCircle(sketch, "E166", {"center": v(-3.6, -6.25) * mm, "radius": 1 * mm});
            skCircle(sketch, "E167", {"center": v(0, -7.22) * mm, "radius": 1 * mm});
            skCircle(sketch, "E168", {"center": v(3.6, -6.25) * mm, "radius": 1 * mm});
            skCircle(sketch, "E169", {"center": v(6.25, -3.6) * mm, "radius": 1 * mm});
            skCircle(sketch, "E170", {"center": v(7.22, 0) * mm, "radius": 1 * mm});
            skCircle(sketch, "E171", {"center": v(6.25, 3.6) * mm, "radius": 1 * mm});
            skCircle(sketch, "E172", {"center": v(3.6, 6.25) * mm, "radius": 1 * mm});
            skCircle(sketch, "E173", {"center": v(0, 7.22) * mm, "radius": 1 * mm});
            skCircle(sketch, "E174", {"center": v(-3.6, 6.25) * mm, "radius": 1 * mm});
            skCircle(sketch, "E175", {"center": v(-6.25, 3.6) * mm, "radius": 1 * mm});
            skCircle(sketch, "E176", {"center": v(-7.22, 0) * mm, "radius": 1 * mm});
            skSolve(sketch);
        }
        {
            var Q0;
            Q0=makeQuery(id+"F16.imprint","IMPRINT",FACE,{"disambiguationData":[TD([[makeQuery(id+"F16.imprint","IMPRINT",EDGE,{"derivedFrom":sQuery(id+"F16.wireOp",EDGE,"E113.0")}),-1.0]])]});
            var Q1;
            Q1=makeQuery(id+"F16.imprint","IMPRINT",FACE,{"disambiguationData":[TD([[makeQuery(id+"F16.imprint","IMPRINT",EDGE,{"derivedFrom":sQuery(id+"F16.wireOp",EDGE,"E114")}),-1.0]])]});
            var Q2;
            Q2=makeQuery(id+"F16.imprint","IMPRINT",FACE,{"disambiguationData":[TD([[makeQuery(id+"F16.imprint","IMPRINT",EDGE,{"derivedFrom":sQuery(id+"F16.wireOp",EDGE,"E115")}),-1.0]])]});
            var Q3;
            Q3=makeQuery(id+"F16.imprint","IMPRINT",FACE,{"disambiguationData":[TD([[makeQuery(id+"F16.imprint","IMPRINT",EDGE,{"derivedFrom":sQuery(id+"F16.wireOp",EDGE,"E116")}),-1.0]])]});
            var Q4;
            Q4=makeQuery(id+"F16.imprint","IMPRINT",FACE,{"disambiguationData":[TD([[makeQuery(id+"F16.imprint","IMPRINT",EDGE,{"derivedFrom":sQuery(id+"F16.wireOp",EDGE,"E117")}),-1.0]])]});
            var Q5;
            Q5=makeQuery(id+"F16.imprint","IMPRINT",FACE,{"disambiguationData":[TD([[makeQuery(id+"F16.imprint","IMPRINT",EDGE,{"derivedFrom":sQuery(id+"F16.wireOp",EDGE,"E118")}),-1.0]])]});
            var Q6;
            Q6=makeQuery(id+"F16.imprint","IMPRINT",FACE,{"disambiguationData":[TD([[makeQuery(id+"F16.imprint","IMPRINT",EDGE,{"derivedFrom":sQuery(id+"F16.wireOp",EDGE,"E119")}),-1.0]])]});
            var Q7;
            Q7=makeQuery(id+"F16.imprint","IMPRINT",FACE,{"disambiguationData":[TD([[makeQuery(id+"F16.imprint","IMPRINT",EDGE,{"derivedFrom":sQuery(id+"F16.wireOp",EDGE,"E120")}),-1.0]])]});
            var Q8;
            Q8=makeQuery(id+"F16.imprint","IMPRINT",FACE,{"disambiguationData":[TD([[makeQuery(id+"F16.imprint","IMPRINT",EDGE,{"derivedFrom":sQuery(id+"F16.wireOp",EDGE,"E121")}),-1.0]])]});
            var Q9;
            Q9=makeQuery(id+"F16.imprint","IMPRINT",FACE,{"disambiguationData":[TD([[makeQuery(id+"F16.imprint","IMPRINT",EDGE,{"derivedFrom":sQuery(id+"F16.wireOp",EDGE,"E122")}),-1.0]])]});
            var Q10;
            Q10=makeQuery(id+"F16.imprint","IMPRINT",FACE,{"disambiguationData":[TD([[makeQuery(id+"F16.imprint","IMPRINT",EDGE,{"derivedFrom":sQuery(id+"F16.wireOp",EDGE,"E123")}),-1.0]])]});
            var Q11;
            Q11=makeQuery(id+"F16.imprint","IMPRINT",FACE,{"disambiguationData":[TD([[makeQuery(id+"F16.imprint","IMPRINT",EDGE,{"derivedFrom":sQuery(id+"F16.wireOp",EDGE,"E124")}),-1.0]])]});
            var Q12;
            Q12=makeQuery(id+"F16.imprint","IMPRINT",FACE,{"disambiguationData":[TD([[makeQuery(id+"F16.imprint","IMPRINT",EDGE,{"derivedFrom":sQuery(id+"F16.wireOp",EDGE,"E125")}),-1.0]])]});
            var Q13;
            Q13=makeQuery(id+"F16.imprint","IMPRINT",FACE,{"disambiguationData":[TD([[makeQuery(id+"F16.imprint","IMPRINT",EDGE,{"derivedFrom":sQuery(id+"F16.wireOp",EDGE,"E126")}),-1.0]])]});
            var Q14;
            Q14=makeQuery(id+"F16.imprint","IMPRINT",FACE,{"disambiguationData":[TD([[makeQuery(id+"F16.imprint","IMPRINT",EDGE,{"derivedFrom":sQuery(id+"F16.wireOp",EDGE,"E116")}),1.0]])]});
            var Q15;
            Q15=makeQuery(id+"F16.imprint","IMPRINT",FACE,{"disambiguationData":[TD([[makeQuery(id+"F16.imprint","IMPRINT",EDGE,{"derivedFrom":sQuery(id+"F16.wireOp",EDGE,"E117")}),1.0]])]});
            var Q16;
            Q16=makeQuery(id+"F16.imprint","IMPRINT",FACE,{"disambiguationData":[TD([[makeQuery(id+"F16.imprint","IMPRINT",EDGE,{"derivedFrom":sQuery(id+"F16.wireOp",EDGE,"E118")}),1.0]])]});
            var Q17;
            Q17=makeQuery(id+"F16.imprint","IMPRINT",FACE,{"disambiguationData":[TD([[makeQuery(id+"F16.imprint","IMPRINT",EDGE,{"derivedFrom":sQuery(id+"F16.wireOp",EDGE,"E119")}),1.0]])]});
            var Q18;
            Q18=makeQuery(id+"F16.imprint","IMPRINT",FACE,{"disambiguationData":[TD([[makeQuery(id+"F16.imprint","IMPRINT",EDGE,{"derivedFrom":sQuery(id+"F16.wireOp",EDGE,"E120")}),1.0]])]});
            var Q19;
            Q19=makeQuery(id+"F16.imprint","IMPRINT",FACE,{"disambiguationData":[TD([[makeQuery(id+"F16.imprint","IMPRINT",EDGE,{"derivedFrom":sQuery(id+"F16.wireOp",EDGE,"E115")}),1.0]])]});
            var Q20;
            Q20=makeQuery(id+"F16.imprint","IMPRINT",FACE,{"disambiguationData":[TD([[makeQuery(id+"F16.imprint","IMPRINT",EDGE,{"derivedFrom":sQuery(id+"F16.wireOp",EDGE,"E126")}),1.0]])]});
            var Q21;
            Q21=makeQuery(id+"F16.imprint","IMPRINT",FACE,{"disambiguationData":[TD([[makeQuery(id+"F16.imprint","IMPRINT",EDGE,{"derivedFrom":sQuery(id+"F16.wireOp",EDGE,"E121")}),1.0]])]});
            var Q22;
            Q22=makeQuery(id+"F16.imprint","IMPRINT",FACE,{"disambiguationData":[TD([[makeQuery(id+"F16.imprint","IMPRINT",EDGE,{"derivedFrom":sQuery(id+"F16.wireOp",EDGE,"E125")}),1.0]])]});
            var Q23;
            Q23=makeQuery(id+"F16.imprint","IMPRINT",FACE,{"disambiguationData":[TD([[makeQuery(id+"F16.imprint","IMPRINT",EDGE,{"derivedFrom":sQuery(id+"F16.wireOp",EDGE,"E124")}),1.0]])]});
            var Q24;
            Q24=makeQuery(id+"F16.imprint","IMPRINT",FACE,{"disambiguationData":[TD([[makeQuery(id+"F16.imprint","IMPRINT",EDGE,{"derivedFrom":sQuery(id+"F16.wireOp",EDGE,"E123")}),1.0]])]});
            var Q25;
            Q25=makeQuery(id+"F16.imprint","IMPRINT",FACE,{"disambiguationData":[TD([[makeQuery(id+"F16.imprint","IMPRINT",EDGE,{"derivedFrom":sQuery(id+"F16.wireOp",EDGE,"E122")}),1.0]])]});
            extrude(context, id + "F17", {"entities" : qUnion([Q0, Q1, Q2, Q3, Q4, Q5, Q6, Q7, Q8, Q9, Q10, Q11, Q12, Q13, Q14, Q15, Q16, Q17, Q18, Q19, Q20, Q21, Q22, Q23, Q24, Q25]), "depth" : 2 * mm});
        }
        {
            var Q0;
            Q0=makeQuery(id+"F16.imprint","IMPRINT",FACE,{"disambiguationData":[TD([[makeQuery(id+"F16.imprint","IMPRINT",EDGE,{"derivedFrom":sQuery(id+"F16.wireOp",EDGE,"E115")}),1.0]])]});
            var Q1;
            Q1=makeQuery(id+"F16.imprint","IMPRINT",FACE,{"disambiguationData":[TD([[makeQuery(id+"F16.imprint","IMPRINT",EDGE,{"derivedFrom":sQuery(id+"F16.wireOp",EDGE,"E126")}),1.0]])]});
            var Q2;
            Q2=makeQuery(id+"F16.imprint","IMPRINT",FACE,{"disambiguationData":[TD([[makeQuery(id+"F16.imprint","IMPRINT",EDGE,{"derivedFrom":sQuery(id+"F16.wireOp",EDGE,"E116")}),1.0]])]});
            var Q3;
            Q3=makeQuery(id+"F16.imprint","IMPRINT",FACE,{"disambiguationData":[TD([[makeQuery(id+"F16.imprint","IMPRINT",EDGE,{"derivedFrom":sQuery(id+"F16.wireOp",EDGE,"E117")}),1.0]])]});
            var Q4;
            Q4=makeQuery(id+"F16.imprint","IMPRINT",FACE,{"disambiguationData":[TD([[makeQuery(id+"F16.imprint","IMPRINT",EDGE,{"derivedFrom":sQuery(id+"F16.wireOp",EDGE,"E118")}),1.0]])]});
            var Q5;
            Q5=makeQuery(id+"F16.imprint","IMPRINT",FACE,{"disambiguationData":[TD([[makeQuery(id+"F16.imprint","IMPRINT",EDGE,{"derivedFrom":sQuery(id+"F16.wireOp",EDGE,"E119")}),1.0]])]});
            var Q6;
            Q6=makeQuery(id+"F16.imprint","IMPRINT",FACE,{"disambiguationData":[TD([[makeQuery(id+"F16.imprint","IMPRINT",EDGE,{"derivedFrom":sQuery(id+"F16.wireOp",EDGE,"E120")}),1.0]])]});
            var Q7;
            Q7=makeQuery(id+"F16.imprint","IMPRINT",FACE,{"disambiguationData":[TD([[makeQuery(id+"F16.imprint","IMPRINT",EDGE,{"derivedFrom":sQuery(id+"F16.wireOp",EDGE,"E121")}),1.0]])]});
            var Q8;
            Q8=makeQuery(id+"F16.imprint","IMPRINT",FACE,{"disambiguationData":[TD([[makeQuery(id+"F16.imprint","IMPRINT",EDGE,{"derivedFrom":sQuery(id+"F16.wireOp",EDGE,"E122")}),1.0]])]});
            var Q9;
            Q9=makeQuery(id+"F16.imprint","IMPRINT",FACE,{"disambiguationData":[TD([[makeQuery(id+"F16.imprint","IMPRINT",EDGE,{"derivedFrom":sQuery(id+"F16.wireOp",EDGE,"E123")}),1.0]])]});
            var Q10;
            Q10=makeQuery(id+"F16.imprint","IMPRINT",FACE,{"disambiguationData":[TD([[makeQuery(id+"F16.imprint","IMPRINT",EDGE,{"derivedFrom":sQuery(id+"F16.wireOp",EDGE,"E124")}),1.0]])]});
            var Q11;
            Q11=makeQuery(id+"F16.imprint","IMPRINT",FACE,{"disambiguationData":[TD([[makeQuery(id+"F16.imprint","IMPRINT",EDGE,{"derivedFrom":sQuery(id+"F16.wireOp",EDGE,"E125")}),1.0]])]});
            extrude(context, id + "F18", {"entities" : qUnion([Q0, Q1, Q2, Q3, Q4, Q5, Q6, Q7, Q8, Q9, Q10, Q11]), "operationType" : NewBodyOperationType.ADD, "oppositeDirection" : true, "depth" : 1.5 * mm});
        }
    });
